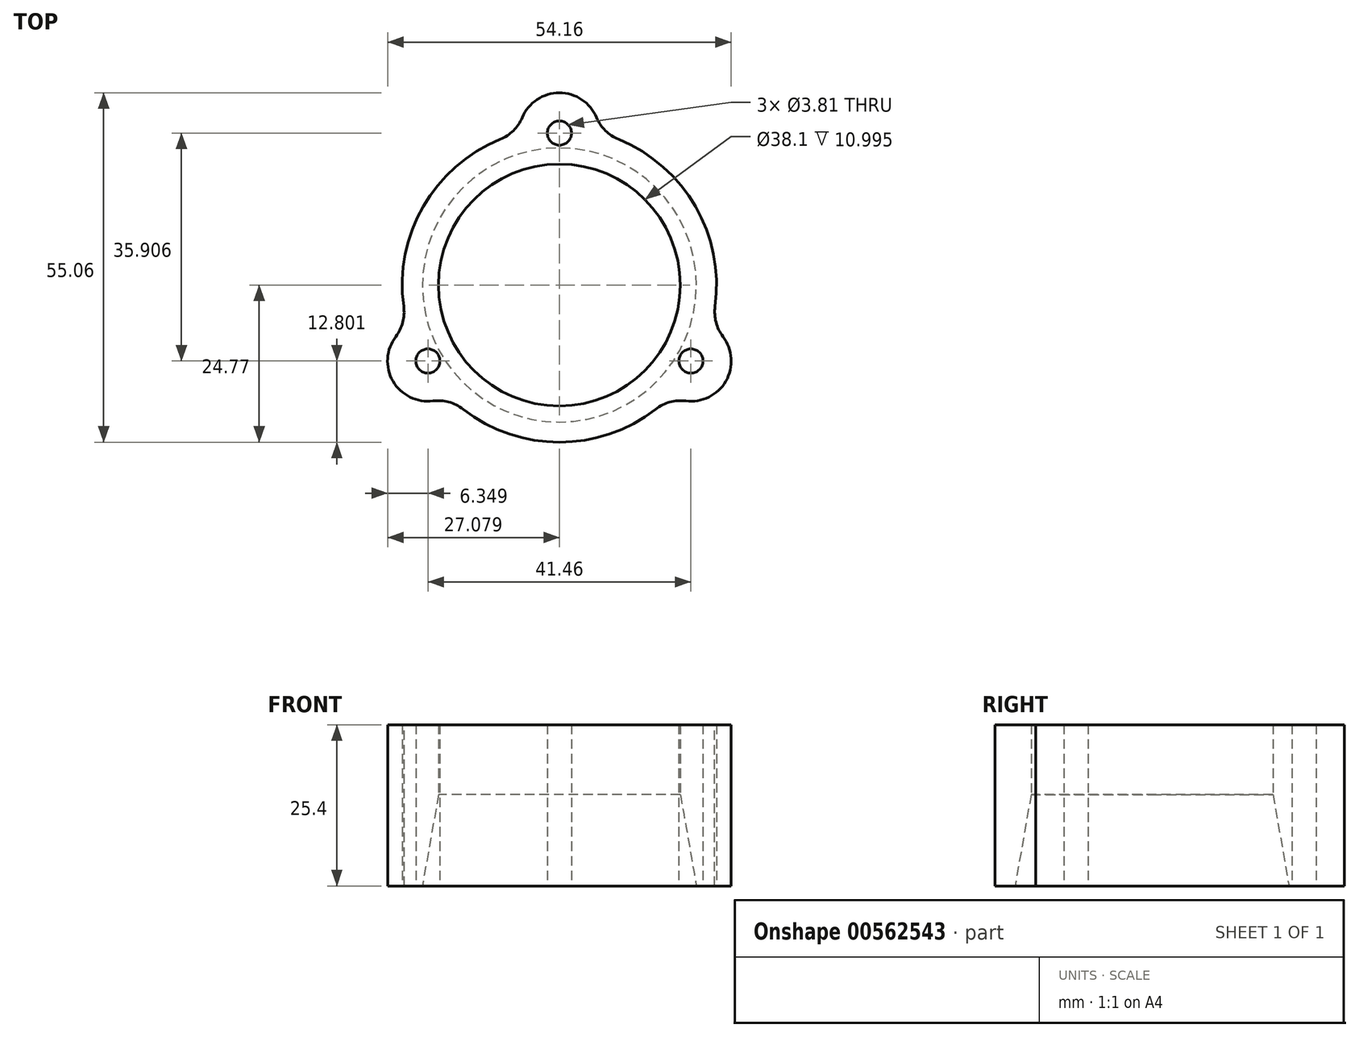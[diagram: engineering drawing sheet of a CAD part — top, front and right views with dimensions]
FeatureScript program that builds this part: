
annotation { "Feature Type Name" : "Feature", "Feature Type Description" : "" }
export const myFeature = defineFeature(function(context is Context, id is Id, definition is map)
    precondition{}
    {
        {
            var Q0;
            Q0=qCreatedBy(makeId("Top.planeOp"),FACE);
            var sketch = newSketch(context, id + "F0", { "sketchPlane" : qUnion([Q0])});
            skCircle(sketch, "E0", {"center": v(-0.2, 1.94) * mm, "radius": 19.05 * mm});
            skCircle(sketch, "E1", {"center": v(-0.2, 1.94) * mm, "radius": 24.77 * mm});
            skLineSegment(sketch, "E2", {"start": v(-0.2, 1.94) * mm, "end": v(-0.2, 44.71) * mm, "construction": true});
            skLineSegment(sketch, "E3", {"start": v(-0.2, 1.94) * mm, "end": v(-43.91, -23.3) * mm, "construction": true});
            skLineSegment(sketch, "E4", {"start": v(-0.2, 1.94) * mm, "end": v(46.7, -25.14) * mm, "construction": true});
            skLineSegment(sketch, "E5", {"start": v(-6.55, 4.1) * mm, "end": v(-6.55, 50.9) * mm, "construction": true});
            skLineSegment(sketch, "E6.MirrorCS", {"start": v(6.15, 4.1) * mm, "end": v(6.15, 50.9) * mm, "construction": true});
            skLineSegment(sketch, "E7", {"start": v(-11.43, 2.79) * mm, "end": v(-49.19, -19) * mm, "construction": true});
            skLineSegment(sketch, "E8.MirrorCS", {"start": v(-5.08, -8.21) * mm, "end": v(-42.84, -30) * mm, "construction": true});
            skLineSegment(sketch, "E9", {"start": v(-0.06, -5.47) * mm, "end": v(38.28, -27.6) * mm, "construction": true});
            skLineSegment(sketch, "E10.MirrorCS", {"start": v(6.29, 5.53) * mm, "end": v(44.63, -16.6) * mm, "construction": true});
            skArc(sketch, "E11", {"start": v(6.15, 25.88) * mm, "mid": v(-0.2, 32.23) * mm, "end": v(-6.55, 25.88) * mm});
            skArc(sketch, "E12", {"start": v(-24.1, -4.53) * mm, "mid": v(-26.43, -13.2) * mm, "end": v(-17.76, -15.53) * mm});
            skArc(sketch, "E13", {"start": v(17.35, -15.53) * mm, "mid": v(26.03, -13.2) * mm, "end": v(23.7, -4.53) * mm});
            skCircle(sketch, "E14", {"center": v(-0.2, 25.88) * mm, "radius": 1.9 * mm});
            skCircle(sketch, "E15", {"center": v(-20.93, -10.03) * mm, "radius": 1.9 * mm});
            skCircle(sketch, "E16", {"center": v(20.53, -10.03) * mm, "radius": 1.9 * mm});
            skSolve(sketch);
        }
        {
            var Q0;
            Q0=makeQuery(id+"F0.imprint","IMPRINT",FACE,{"disambiguationData":[TD([[makeQuery(id+"F0.imprint","IMPRINT",EDGE,{"derivedFrom":sQuery(id+"F0.wireOp",EDGE,"E0")}),-1.0]])]});
            var Q1;
            {var subQ0=sQuery(id+"F0.wireOp",EDGE,"E11");Q1=makeQuery(id+"F0.imprint","IMPRINT",FACE,{"disambiguationData":[TD([[makeQuery(id+"F0.imprint","IMPRINT",EDGE,{"derivedFrom":subQ0}),1.0]])]});}
            var Q2;
            {var subQ0=sQuery(id+"F0.wireOp",EDGE,"E13");Q2=makeQuery(id+"F0.imprint","IMPRINT",FACE,{"disambiguationData":[TD([[makeQuery(id+"F0.imprint","IMPRINT",EDGE,{"derivedFrom":subQ0}),1.0]])]});}
            var Q3;
            {var subQ0=sQuery(id+"F0.wireOp",EDGE,"E12");Q3=makeQuery(id+"F0.imprint","IMPRINT",FACE,{"disambiguationData":[TD([[makeQuery(id+"F0.imprint","IMPRINT",EDGE,{"derivedFrom":subQ0}),1.0]])]});}
            extrude(context, id + "F1", {"entities" : qUnion([Q0, Q1, Q2, Q3]), "depth" : 25.4 * mm, "offsetDistance" : 25.4 * mm});
        }
        {
            var Q0;
            {var subQ0=sQuery(id+"F0.wireOp",EDGE,"E12");var subQ1=sQuery(id+"F0.wireOp",EDGE,"E1");Q0=makeQuery(id+"F1.opExtrude","SWEPT_EDGE",EDGE,{"disambiguationData":[OSD([subQ1,subQ0]),TDD([makeQuery(id+"F0.imprint","INTERSECT",VERTEX,{"disambiguationData":[OD(1.0)],"derivedFrom":[subQ1,subQ0]})])]});}
            var Q1;
            {var subQ0=sQuery(id+"F0.wireOp",EDGE,"E13");var subQ1=sQuery(id+"F0.wireOp",EDGE,"E1");Q1=makeQuery(id+"F1.opExtrude","SWEPT_EDGE",EDGE,{"disambiguationData":[OSD([subQ1,subQ0]),TDD([makeQuery(id+"F0.imprint","INTERSECT",VERTEX,{"disambiguationData":[OD(0.0)],"derivedFrom":[subQ1,subQ0]})])]});}
            var Q2;
            {var subQ0=sQuery(id+"F0.wireOp",EDGE,"E12");var subQ1=sQuery(id+"F0.wireOp",EDGE,"E1");Q2=makeQuery(id+"F1.opExtrude","SWEPT_EDGE",EDGE,{"disambiguationData":[OSD([subQ1,subQ0]),TDD([makeQuery(id+"F0.imprint","INTERSECT",VERTEX,{"disambiguationData":[OD(0.0)],"derivedFrom":[subQ1,subQ0]})])]});}
            var Q3;
            {var subQ0=sQuery(id+"F0.wireOp",EDGE,"E11");var subQ1=sQuery(id+"F0.wireOp",EDGE,"E1");Q3=makeQuery(id+"F1.opExtrude","SWEPT_EDGE",EDGE,{"disambiguationData":[OSD([subQ1,subQ0]),TDD([makeQuery(id+"F0.imprint","INTERSECT",VERTEX,{"disambiguationData":[OD(1.0)],"derivedFrom":[subQ1,subQ0]})])]});}
            var Q4;
            {var subQ0=sQuery(id+"F0.wireOp",EDGE,"E11");var subQ1=sQuery(id+"F0.wireOp",EDGE,"E1");Q4=makeQuery(id+"F1.opExtrude","SWEPT_EDGE",EDGE,{"disambiguationData":[OSD([subQ1,subQ0]),TDD([makeQuery(id+"F0.imprint","INTERSECT",VERTEX,{"disambiguationData":[OD(0.0)],"derivedFrom":[subQ1,subQ0]})])]});}
            var Q5;
            {var subQ0=sQuery(id+"F0.wireOp",EDGE,"E13");var subQ1=sQuery(id+"F0.wireOp",EDGE,"E1");Q5=makeQuery(id+"F1.opExtrude","SWEPT_EDGE",EDGE,{"disambiguationData":[OSD([subQ1,subQ0]),TDD([makeQuery(id+"F0.imprint","INTERSECT",VERTEX,{"disambiguationData":[OD(1.0)],"derivedFrom":[subQ1,subQ0]})])]});}
            fillet(context, id + "F2", {"entities" : qUnion([Q0, Q1, Q2, Q3, Q4, Q5]), "radius" : 6.35 * mm, "tangentPropagation" : true, "allowEdgeOverflow" : false});
        }
        {
            var Q0;
            Q0=makeQuery(id+"F1.opExtrude","CAP_EDGE",EDGE,{"disambiguationData":[OSD([sQuery(id+"F0.wireOp",EDGE,"E0")])],"isStart":true});
            chamfer(context, id + "F3", {"entities" : qUnion([Q0]), "chamferType" : ChamferType.OFFSET_ANGLE, "width" : 2.54 * mm, "oppositeDirection" : false, "angle" : 80 * degree, "tangentPropagation" : true});
        }
    });
